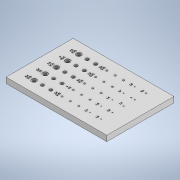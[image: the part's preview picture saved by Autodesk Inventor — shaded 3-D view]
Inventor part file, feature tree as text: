
AUTODESK INVENTOR PART (.ipt)
format: ipt  version: 2020.3 (Build 243373000, 373)  size: 2,556,416 bytes
history: native  units: mm
features: hole x35, extrude x1, emboss x1
ambient origin geometry x8: Origin, YZ Plane, XZ Plane, XY Plane, X Axis, Y Axis, Z Axis, Center Point
bodies: Solid1 (feature_tree)
feature tree (37):
  extrude  "Extrusion1"  Depth=10.0mm
  hole  "Hole1"  [1 undecoded]
  hole  "Hole2"  [1 undecoded]
  hole  "Hole3"  [1 undecoded]
  hole  "Hole4"  [1 undecoded]
  hole  "Hole5"  [1 undecoded]
  hole  "Hole6"  [1 undecoded]
  hole  "Hole7"  [1 undecoded]
  hole  "Hole8"  [1 undecoded]
  hole  "Hole9"  [1 undecoded]
  hole  "Hole10"  [1 undecoded]
  hole  "Hole11"  [1 undecoded]
  hole  "Hole12"  [1 undecoded]
  hole  "Hole13"  [1 undecoded]
  hole  "Hole14"  [1 undecoded]
  hole  "Hole15"  [1 undecoded]
  hole  "Hole16"  [1 undecoded]
  hole  "Hole17"  [1 undecoded]
  hole  "Hole18"  [1 undecoded]
  hole  "Hole19"  [1 undecoded]
  hole  "Hole20"  [1 undecoded]
  hole  "Hole21"  [1 undecoded]
  hole  "Hole22"  [1 undecoded]
  hole  "Hole23"  [1 undecoded]
  hole  "Hole24"  [1 undecoded]
  hole  "Hole25"  [1 undecoded]
  hole  "Hole26"  [1 undecoded]
  hole  "Hole27"  [1 undecoded]
  hole  "Hole28"  [1 undecoded]
  hole  "Hole29"  [1 undecoded]
  hole  "Hole30"  [1 undecoded]
  hole  "Hole31"  [1 undecoded]
  hole  "Hole32"  [1 undecoded]
  hole  "Hole33"  [1 undecoded]
  hole  "Hole34"  [1 undecoded]
  hole  "Hole35"  [1 undecoded]
  emboss  "Emboss1"
note: 35 required parameter values undecoded (feature->parameter linkage not recoverable at this tier; creation-order binding heuristic only, values carry confidence <= 0.55)
